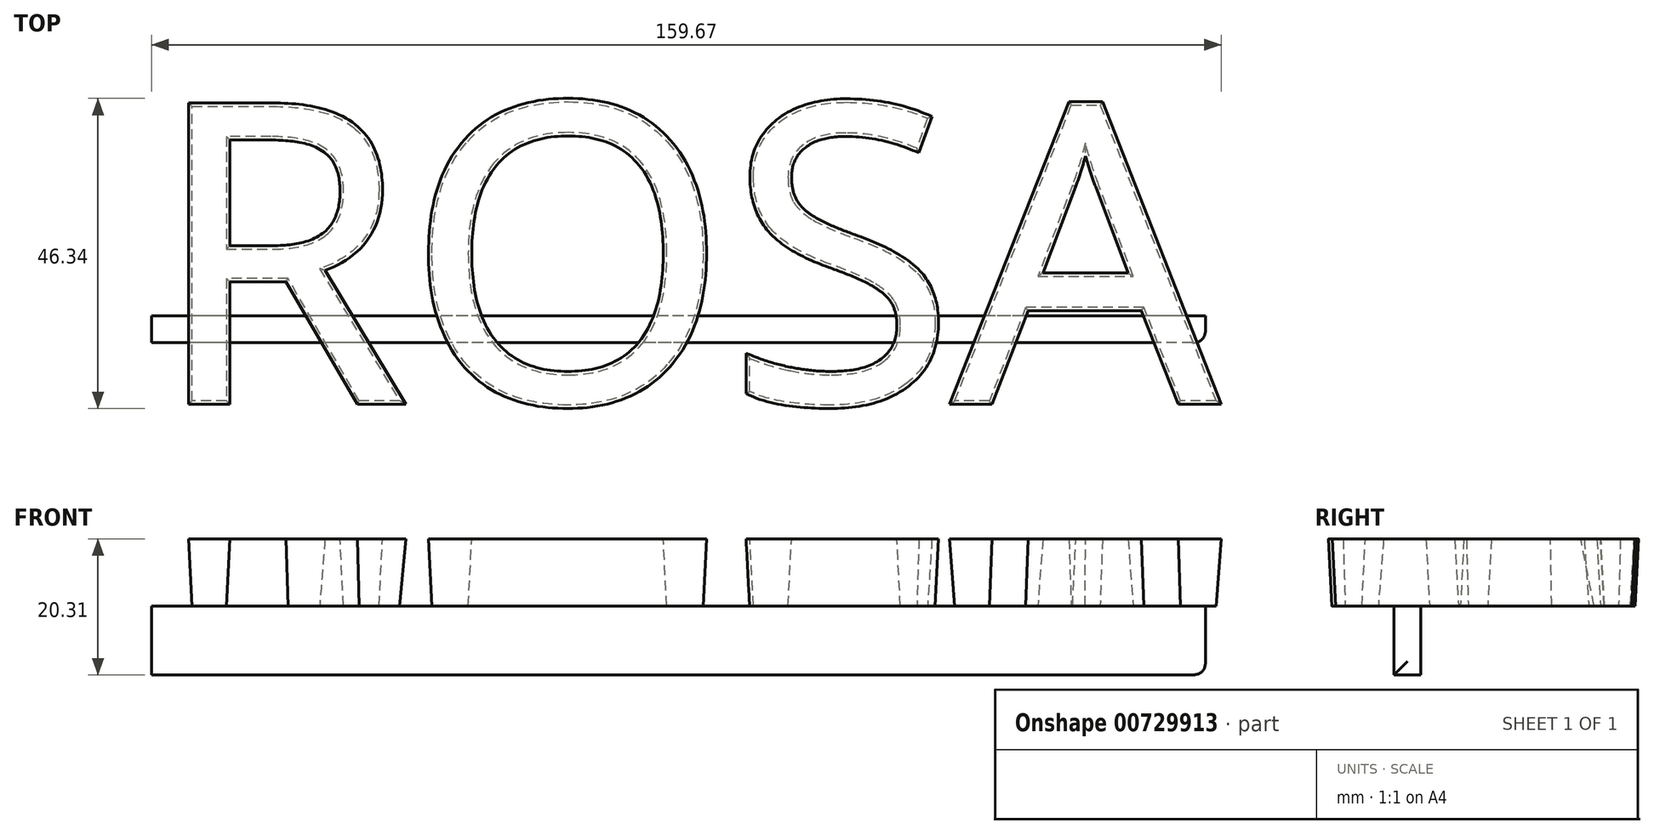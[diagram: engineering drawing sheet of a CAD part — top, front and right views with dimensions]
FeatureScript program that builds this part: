
annotation { "Feature Type Name" : "Feature", "Feature Type Description" : "" }
export const myFeature = defineFeature(function(context is Context, id is Id, definition is map)
    precondition{}
    {
        {
            var Q0;
            Q0=qCreatedBy(makeId("Top.planeOp"),FACE);
            var sketch = newSketch(context, id + "F0", { "sketchPlane" : qUnion([Q0])});
            skText(sketch, "E0", { "text": "ROSA", "fontName": "OpenSans-Regular.ttf"});
            const initialGuessF0  = {"E0": [0, -0.00868, 1, 0, 0.04437]};
            skSetInitialGuess(sketch, initialGuessF0);
            skSolve(sketch);
        }
        {
            var Q0;
            Q0 = qSketchRegion(id + "F0", true);
            extrude(context, id + "F1", {"entities" : qUnion([Q0]), "depth" : 10 * mm, "offsetDistance" : 25.4 * mm, "hasDraft" : true, "draftAngle" : 3 * degree});
        }
        {
            var Q0;
            Q0=qCreatedBy(makeId("Front.planeOp"),FACE);
            var sketch = newSketch(context, id + "F2", { "sketchPlane" : qUnion([Q0])});
            skLineSegment(sketch, "E1.bottom", {"start": v(157.34, 0) * mm, "end": v(0, 0) * mm});
            skLineSegment(sketch, "E1.top", {"start": v(157.34, -10.31) * mm, "end": v(0, -10.31) * mm});
            skLineSegment(sketch, "E1.left", {"start": v(157.34, 0) * mm, "end": v(157.34, -10.31) * mm});
            skLineSegment(sketch, "E1.right", {"start": v(0, 0) * mm, "end": v(0, -10.31) * mm});
            skSolve(sketch);
        }
        {
            var Q0;
            Q0 = qSketchRegion(id + "F2", true);
            extrude(context, id + "F3", {"entities" : qUnion([Q0]), "oppositeDirection" : true, "depth" : 4 * mm, "offsetDistance" : 25.4 * mm});
        }
        {
            var Q0;
            Q0=makeQuery(id+"F3.opExtrude","CAP_EDGE",EDGE,{"disambiguationData":[OSD([sQuery(id+"F2.wireOp",EDGE,"E1.left")])],"isStart":true});
            var Q1;
            Q1=makeQuery(id+"F3.opExtrude","SWEPT_EDGE",EDGE,{"disambiguationData":[OSD([sQuery(id+"F2.wireOp",EDGE,"E1.top"),sQuery(id+"F2.wireOp",EDGE,"E1.left")])]});
            fillet(context, id + "F4", {"entities" : qUnion([Q0, Q1]), "radius" : 2 * mm, "rho" : 0.5, "crossSection" : FilletCrossSection.CONIC, "allowEdgeOverflow" : false});
        }
    });
